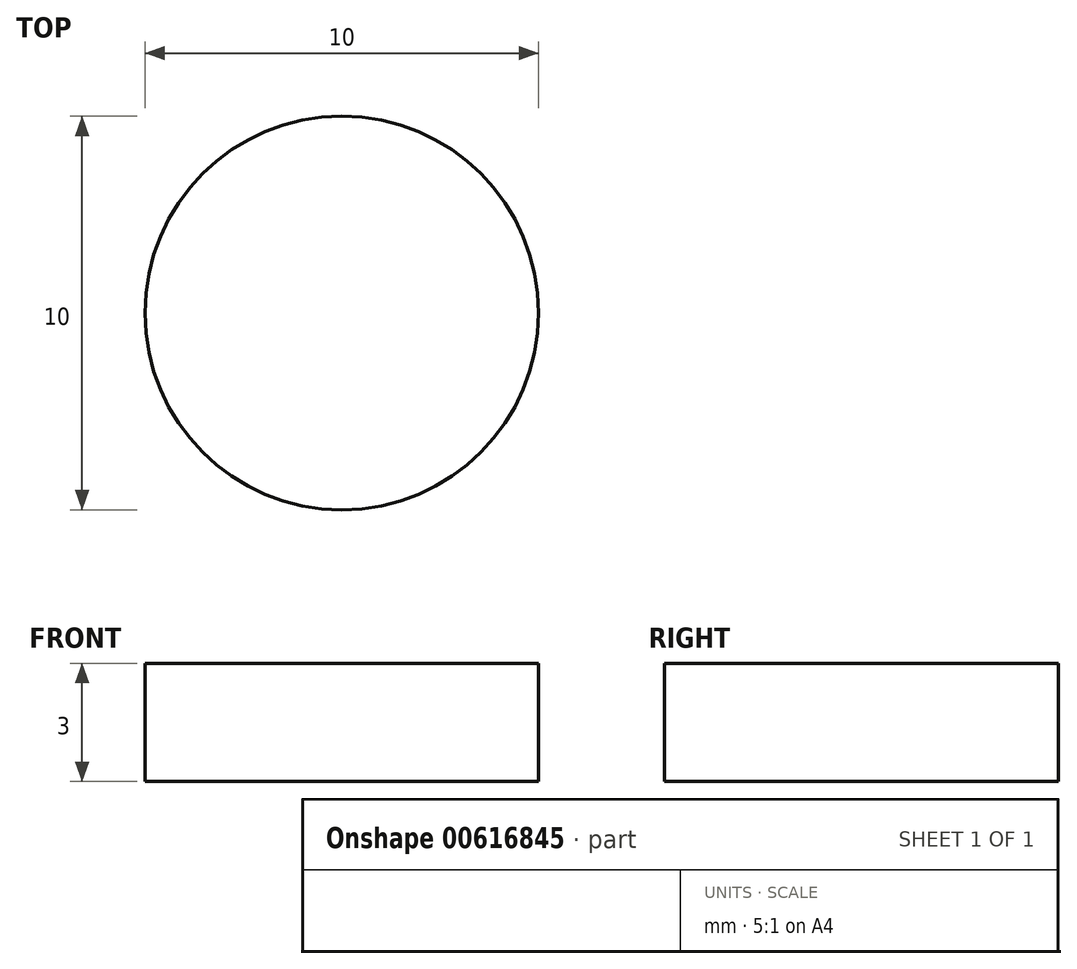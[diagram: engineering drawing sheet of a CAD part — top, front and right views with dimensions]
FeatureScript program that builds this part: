
annotation { "Feature Type Name" : "Feature", "Feature Type Description" : "" }
export const myFeature = defineFeature(function(context is Context, id is Id, definition is map)
    precondition{}
    {
        {
            var Q0;
            Q0=qCreatedBy(makeId("Top.planeOp"),FACE);
            var sketch = newSketch(context, id + "F0", { "sketchPlane" : qUnion([Q0])});
            skCircle(sketch, "E0", {"center": v(0, 0) * mm, "radius": 5 * mm});
            skSolve(sketch);
        }
        {
            var Q0;
            Q0 = qSketchRegion(id + "F0", true);
            extrude(context, id + "F1", {"entities" : qUnion([Q0]), "depth" : 3 * mm, "offsetDistance" : 25 * mm});
        }
    });
